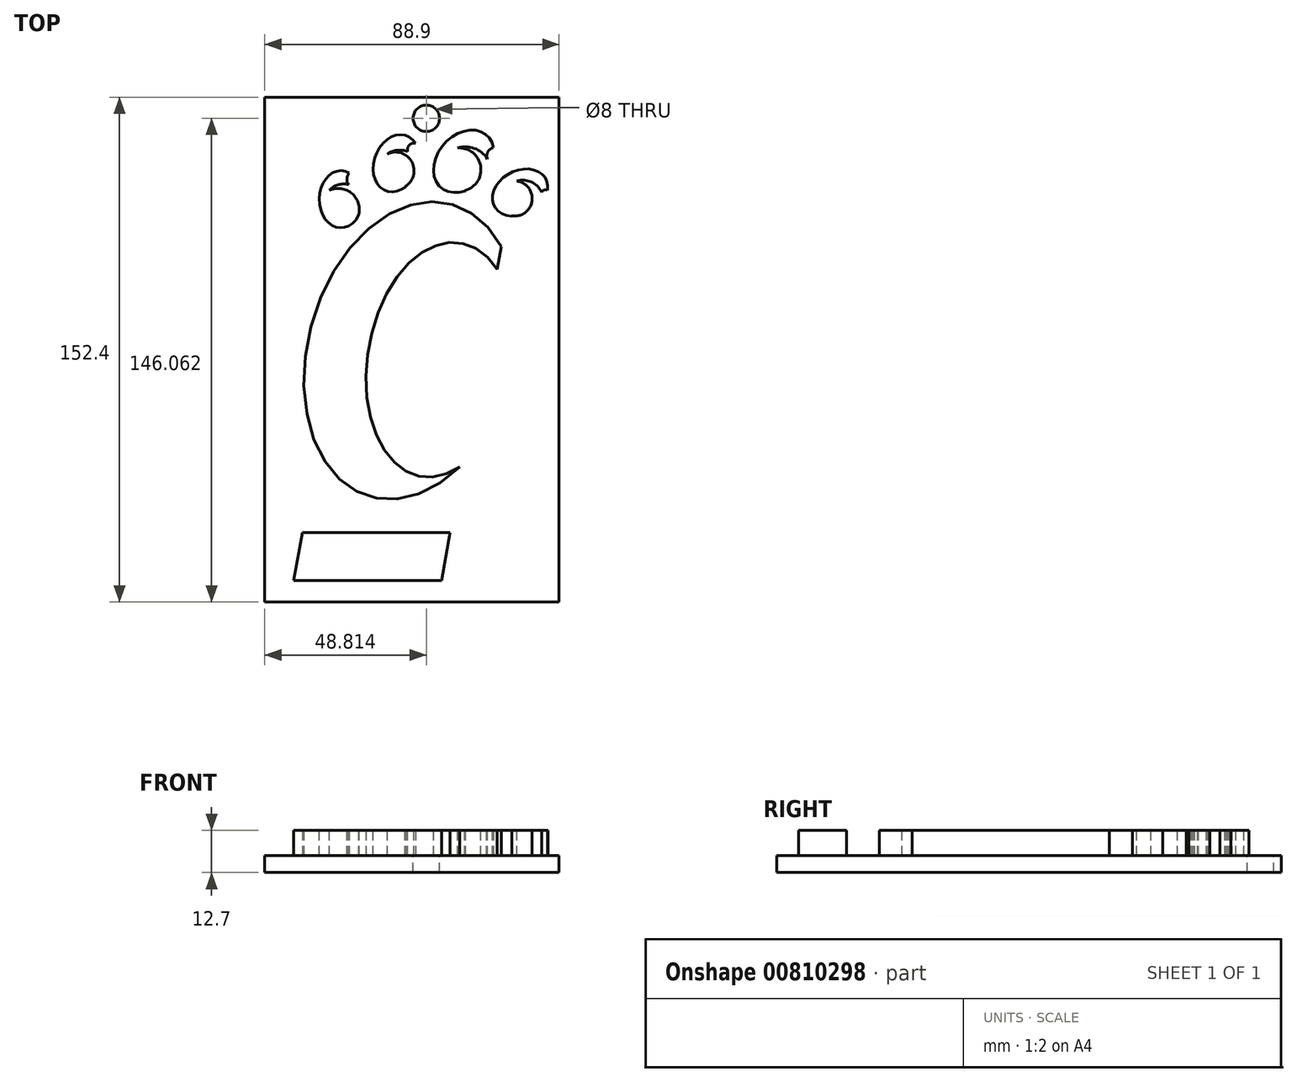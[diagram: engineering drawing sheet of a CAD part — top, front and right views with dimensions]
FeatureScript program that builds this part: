
annotation { "Feature Type Name" : "Feature", "Feature Type Description" : "" }
export const myFeature = defineFeature(function(context is Context, id is Id, definition is map)
    precondition{}
    {
        {
            var Q0;
            Q0=qCreatedBy(makeId("Top.planeOp"),FACE);
            var sketch = newSketch(context, id + "F0", { "sketchPlane" : qUnion([Q0])});
            skLineSegment(sketch, "E0.bottom", {"start": v(-44.23, 76.48) * mm, "end": v(44.67, 76.48) * mm});
            skLineSegment(sketch, "E0.top", {"start": v(-44.23, -75.92) * mm, "end": v(44.67, -75.92) * mm});
            skLineSegment(sketch, "E0.left", {"start": v(-44.23, 76.48) * mm, "end": v(-44.23, -75.92) * mm});
            skLineSegment(sketch, "E0.right", {"start": v(44.67, 76.48) * mm, "end": v(44.67, -75.92) * mm});
            skSolve(sketch);
        }
        {
            var Q0;
            Q0 = qSketchRegion(id + "F0", true);
            extrude(context, id + "F1", {"entities" : qUnion([Q0]), "depth" : 5.08 * mm, "offsetDistance" : 25.4 * mm});
        }
        {
            var Q0;
            Q0=makeQuery(id+"F1.opExtrude","CAP_FACE",FACE,{"disambiguationData":[OSD([sQuery(id+"F0.wireOp",EDGE,"E0.bottom"),sQuery(id+"F0.wireOp",EDGE,"E0.top"),sQuery(id+"F0.wireOp",EDGE,"E0.left"),sQuery(id+"F0.wireOp",EDGE,"E0.right")])],"isStart":false});
            var sketch = newSketch(context, id + "F2", { "sketchPlane" : qUnion([Q0])});
            skEllipse(sketch, "E1", {"center": v(0, 0) * mm, "majorRadius": 45.85 * mm, "minorRadius": 31.11 * mm, "majorAxis": v(0.27, 0.96)});
            skLineSegment(sketch, "E2", {"start": v(11.98, -62.3) * mm, "end": v(41.78, 26.62) * mm, "construction": true});
            skLineSegment(sketch, "E3", {"start": v(-32.4, 56.06) * mm, "end": v(-32.4, -93.93) * mm, "construction": true});
            skEllipse(sketch, "E4", {"center": v(-21.23, 45.7) * mm, "majorRadius": 8.63 * mm, "minorRadius": 6.5 * mm, "majorAxis": v(0, 1)});
            skLineSegment(sketch, "E5.bottom", {"start": v(-32.4, -54.94) * mm, "end": v(14.01, -54.94) * mm});
            skLineSegment(sketch, "E5.top", {"start": v(-32.4, -69.38) * mm, "end": v(14.01, -69.38) * mm});
            skLineSegment(sketch, "E5.left", {"start": v(-32.4, -54.94) * mm, "end": v(-32.4, -69.38) * mm});
            skLineSegment(sketch, "E5.right", {"start": v(14.01, -54.94) * mm, "end": v(14.01, -69.38) * mm});
            skLineSegment(sketch, "E6", {"start": v(-32.4, -54.94) * mm, "end": v(-37.64, -54.94) * mm});
            skLineSegment(sketch, "E7", {"start": v(-37.64, -54.94) * mm, "end": v(-37.64, -69.38) * mm});
            skLineSegment(sketch, "E8", {"start": v(-37.64, -69.38) * mm, "end": v(-32.4, -69.38) * mm});
            skEllipse(sketch, "E9.1.0", {"center": v(-4.51, 56.55) * mm, "majorRadius": 8.86 * mm, "minorRadius": 6.68 * mm, "majorAxis": v(0.36, 0.93)});
            skEllipse(sketch, "E9.2.0", {"center": v(15.88, 57.16) * mm, "majorRadius": 10.5 * mm, "minorRadius": 7.91 * mm, "majorAxis": v(0.66, 0.75)});
            skEllipse(sketch, "E9.3.0", {"center": v(32.92, 47.72) * mm, "majorRadius": 8.78 * mm, "minorRadius": 6.62 * mm, "majorAxis": v(0.89, 0.46)});
            skPoint(sketch, "E9.center", {"position": v(-1.4, 3) * mm});
            skLineSegment(sketch, "E9.anchor1", {"start": v(-1.4, 3) * mm, "end": v(-21.23, 45.7) * mm, "construction": true});
            skLineSegment(sketch, "E9.anchor2", {"start": v(-1.4, 3) * mm, "end": v(32.92, 47.72) * mm, "construction": true});
            skSolve(sketch);
        }
        {
            var Q0;
            Q0 = qSketchRegion(id + "F2", true);
            extrude(context, id + "F3", {"entities" : qUnion([Q0]), "operationType" : NewBodyOperationType.ADD, "depth" : 7.62 * mm, "offsetDistance" : 25.4 * mm});
        }
        {
            var Q0;
            Q0=makeQuery(id+"F3.opExtrude","CAP_FACE",FACE,{"disambiguationData":[OSD([sQuery(id+"F2.wireOp",EDGE,"E1")])],"isStart":false});
            var sketch = newSketch(context, id + "F4", { "sketchPlane" : qUnion([Q0])});
            skEllipse(sketch, "E10", {"center": v(8.96, -2.77) * mm, "majorRadius": 35.74 * mm, "minorRadius": 22.1 * mm, "majorAxis": v(0.17, 0.99)});
            skLineSegment(sketch, "E11", {"start": v(28.36, 37.68) * mm, "end": v(8.92, -70.85) * mm, "construction": true});
            skLineSegment(sketch, "E12", {"start": v(8.92, -70.85) * mm, "end": v(28.36, 37.68) * mm});
            skLineSegment(sketch, "E13", {"start": v(28.36, 37.68) * mm, "end": v(40.84, 41.03) * mm});
            skLineSegment(sketch, "E14", {"start": v(40.84, 41.03) * mm, "end": v(33.24, -73.97) * mm});
            skLineSegment(sketch, "E15", {"start": v(33.24, -73.97) * mm, "end": v(8.92, -70.85) * mm});
            skLineSegment(sketch, "E16", {"start": v(-35.94, -72.2) * mm, "end": v(-30.87, -43.87) * mm});
            skLineSegment(sketch, "E17", {"start": v(-32.74, 21.4) * mm, "end": v(-32.74, -53.48) * mm, "construction": true});
            skLineSegment(sketch, "E18", {"start": v(-30.87, -43.87) * mm, "end": v(-41.57, -48.61) * mm});
            skLineSegment(sketch, "E19", {"start": v(-41.57, -48.61) * mm, "end": v(-41.57, -74.48) * mm});
            skLineSegment(sketch, "E20", {"start": v(-41.57, -74.48) * mm, "end": v(-35.94, -72.2) * mm});
            skArc(sketch, "E21", {"start": v(-18.65, 53.68) * mm, "mid": v(-19.4, 51.93) * mm, "end": v(-18.92, 50.1) * mm});
            skArc(sketch, "E22", {"start": v(-18.92, 50.1) * mm, "mid": v(-22.09, 50.08) * mm, "end": v(-24.75, 48.38) * mm});
            skArc(sketch, "E23", {"start": v(-16, 40.42) * mm, "mid": v(-17.73, 47.31) * mm, "end": v(-24.75, 48.38) * mm});
            skLineSegment(sketch, "E24", {"start": v(-18.65, 53.68) * mm, "end": v(-16.38, 52.59) * mm});
            skLineSegment(sketch, "E25", {"start": v(-16.38, 52.59) * mm, "end": v(-13.45, 46.5) * mm});
            skLineSegment(sketch, "E26", {"start": v(-13.45, 46.5) * mm, "end": v(-14.73, 41.48) * mm});
            skLineSegment(sketch, "E27", {"start": v(-14.73, 41.48) * mm, "end": v(-16, 40.42) * mm});
            skArc(sketch, "E28", {"start": v(1.33, 62.63) * mm, "mid": v(-0.56, 62.05) * mm, "end": v(-1.08, 60.14) * mm});
            skArc(sketch, "E29", {"start": v(-1.08, 60.14) * mm, "mid": v(-4.22, 60.5) * mm, "end": v(-7.18, 59.39) * mm});
            skArc(sketch, "E30", {"start": v(-1.83, 49.52) * mm, "mid": v(0.2, 57) * mm, "end": v(-7.18, 59.39) * mm});
            skArc(sketch, "E31", {"start": v(25, 61.26) * mm, "mid": v(23.18, 60.05) * mm, "end": v(23.03, 57.87) * mm});
            skArc(sketch, "E32", {"start": v(23.03, 57.87) * mm, "mid": v(19.11, 61.05) * mm, "end": v(14.07, 61.19) * mm});
            skArc(sketch, "E33", {"start": v(16.25, 48.3) * mm, "mid": v(20.99, 55.73) * mm, "end": v(14.07, 61.19) * mm});
            skArc(sketch, "E34", {"start": v(41.27, 48.46) * mm, "mid": v(40.18, 48.51) * mm, "end": v(39.39, 47.78) * mm});
            skArc(sketch, "E35", {"start": v(39.39, 47.78) * mm, "mid": v(36.3, 50.9) * mm, "end": v(31.93, 51.17) * mm});
            skArc(sketch, "E36", {"start": v(30.34, 40.7) * mm, "mid": v(36.5, 45.12) * mm, "end": v(31.93, 51.17) * mm});
            skLineSegment(sketch, "E37", {"start": v(1.33, 62.63) * mm, "end": v(4.84, 59.27) * mm});
            skLineSegment(sketch, "E38", {"start": v(4.84, 59.27) * mm, "end": v(1.95, 48.96) * mm});
            skLineSegment(sketch, "E39", {"start": v(1.95, 48.96) * mm, "end": v(-1.83, 49.52) * mm});
            skLineSegment(sketch, "E40", {"start": v(25, 61.26) * mm, "end": v(28.48, 57.82) * mm});
            skLineSegment(sketch, "E41", {"start": v(28.48, 57.82) * mm, "end": v(20.24, 45.4) * mm});
            skLineSegment(sketch, "E42", {"start": v(20.24, 45.4) * mm, "end": v(16.25, 48.3) * mm});
            skLineSegment(sketch, "E43", {"start": v(41.27, 48.46) * mm, "end": v(42.75, 47.75) * mm});
            skLineSegment(sketch, "E44", {"start": v(42.75, 47.75) * mm, "end": v(41.27, 44.64) * mm});
            skLineSegment(sketch, "E45", {"start": v(41.27, 44.64) * mm, "end": v(37.75, 40.96) * mm});
            skLineSegment(sketch, "E46", {"start": v(37.75, 40.96) * mm, "end": v(31.19, 38.77) * mm});
            skLineSegment(sketch, "E47", {"start": v(31.19, 38.77) * mm, "end": v(30.3, 40.66) * mm});
            skLineSegment(sketch, "E48", {"start": v(30.34, 40.7) * mm, "end": v(31.19, 38.77) * mm});
            skLineSegment(sketch, "E49", {"start": v(31.19, 38.77) * mm, "end": v(37.75, 40.96) * mm});
            skLineSegment(sketch, "E50", {"start": v(41.27, 44.64) * mm, "end": v(42.75, 47.75) * mm});
            skSolve(sketch);
        }
        {
            var Q0;
            Q0 = qSketchRegion(id + "F4", true);
            extrude(context, id + "F5", {"entities" : qUnion([Q0]), "operationType" : NewBodyOperationType.REMOVE, "oppositeDirection" : true, "depth" : 7.62 * mm, "offsetDistance" : 25.4 * mm});
        }
        {
            var Q0;
            Q0=makeQuery(id+"F5.boolean.opBoolean","MERGE",FACE,{"derivedFrom":[makeQuery(id+"F1.opExtrude","CAP_FACE",FACE,{"disambiguationData":[OSD([sQuery(id+"F0.wireOp",EDGE,"E0.bottom"),sQuery(id+"F0.wireOp",EDGE,"E0.top"),sQuery(id+"F0.wireOp",EDGE,"E0.left"),sQuery(id+"F0.wireOp",EDGE,"E0.right")])],"isStart":false}),makeQuery(id+"F5.opExtrude","CAP_FACE",FACE,{"disambiguationData":[OSD([sQuery(id+"F4.wireOp",EDGE,"E10"),sQuery(id+"F4.wireOp",EDGE,"E12"),sQuery(id+"F4.wireOp",EDGE,"E13"),sQuery(id+"F4.wireOp",EDGE,"E14"),sQuery(id+"F4.wireOp",EDGE,"E15")])],"isStart":false}),makeQuery(id+"F5.opExtrude","CAP_FACE",FACE,{"disambiguationData":[OSD([sQuery(id+"F4.wireOp",EDGE,"E16"),sQuery(id+"F4.wireOp",EDGE,"E18"),sQuery(id+"F4.wireOp",EDGE,"E19"),sQuery(id+"F4.wireOp",EDGE,"E20")])],"isStart":false}),makeQuery(id+"F5.opExtrude","CAP_FACE",FACE,{"disambiguationData":[OSD([sQuery(id+"F4.wireOp",EDGE,"E21"),sQuery(id+"F4.wireOp",EDGE,"E22"),sQuery(id+"F4.wireOp",EDGE,"E23"),sQuery(id+"F4.wireOp",EDGE,"E24"),sQuery(id+"F4.wireOp",EDGE,"E25"),sQuery(id+"F4.wireOp",EDGE,"E26"),sQuery(id+"F4.wireOp",EDGE,"E27")])],"isStart":false}),makeQuery(id+"F5.opExtrude","CAP_FACE",FACE,{"disambiguationData":[OSD([sQuery(id+"F4.wireOp",EDGE,"E28"),sQuery(id+"F4.wireOp",EDGE,"E29"),sQuery(id+"F4.wireOp",EDGE,"E30"),sQuery(id+"F4.wireOp",EDGE,"E37"),sQuery(id+"F4.wireOp",EDGE,"E38"),sQuery(id+"F4.wireOp",EDGE,"E39")])],"isStart":false}),makeQuery(id+"F5.opExtrude","CAP_FACE",FACE,{"disambiguationData":[OSD([sQuery(id+"F4.wireOp",EDGE,"E31"),sQuery(id+"F4.wireOp",EDGE,"E32"),sQuery(id+"F4.wireOp",EDGE,"E33"),sQuery(id+"F4.wireOp",EDGE,"E40"),sQuery(id+"F4.wireOp",EDGE,"E41"),sQuery(id+"F4.wireOp",EDGE,"E42")])],"isStart":false}),makeQuery(id+"F5.opExtrude","CAP_FACE",FACE,{"disambiguationData":[OSD([sQuery(id+"F4.wireOp",EDGE,"E34"),sQuery(id+"F4.wireOp",EDGE,"E35"),sQuery(id+"F4.wireOp",EDGE,"E36"),sQuery(id+"F4.wireOp",EDGE,"E48"),sQuery(id+"F4.wireOp",EDGE,"E49"),sQuery(id+"F4.wireOp",EDGE,"E45"),sQuery(id+"F4.wireOp",EDGE,"E50"),sQuery(id+"F4.wireOp",EDGE,"E43")])],"isStart":false})]});
            var sketch = newSketch(context, id + "F6", { "sketchPlane" : qUnion([Q0])});
            skCircle(sketch, "E51", {"center": v(4.58, 70.14) * mm, "radius": 4 * mm});
            skSolve(sketch);
        }
        {
            var Q0;
            Q0 = qSketchRegion(id + "F6", true);
            extrude(context, id + "F7", {"entities" : qUnion([Q0]), "operationType" : NewBodyOperationType.REMOVE, "oppositeDirection" : true, "depth" : 25.4 * mm, "offsetDistance" : 25.4 * mm});
        }
    });
